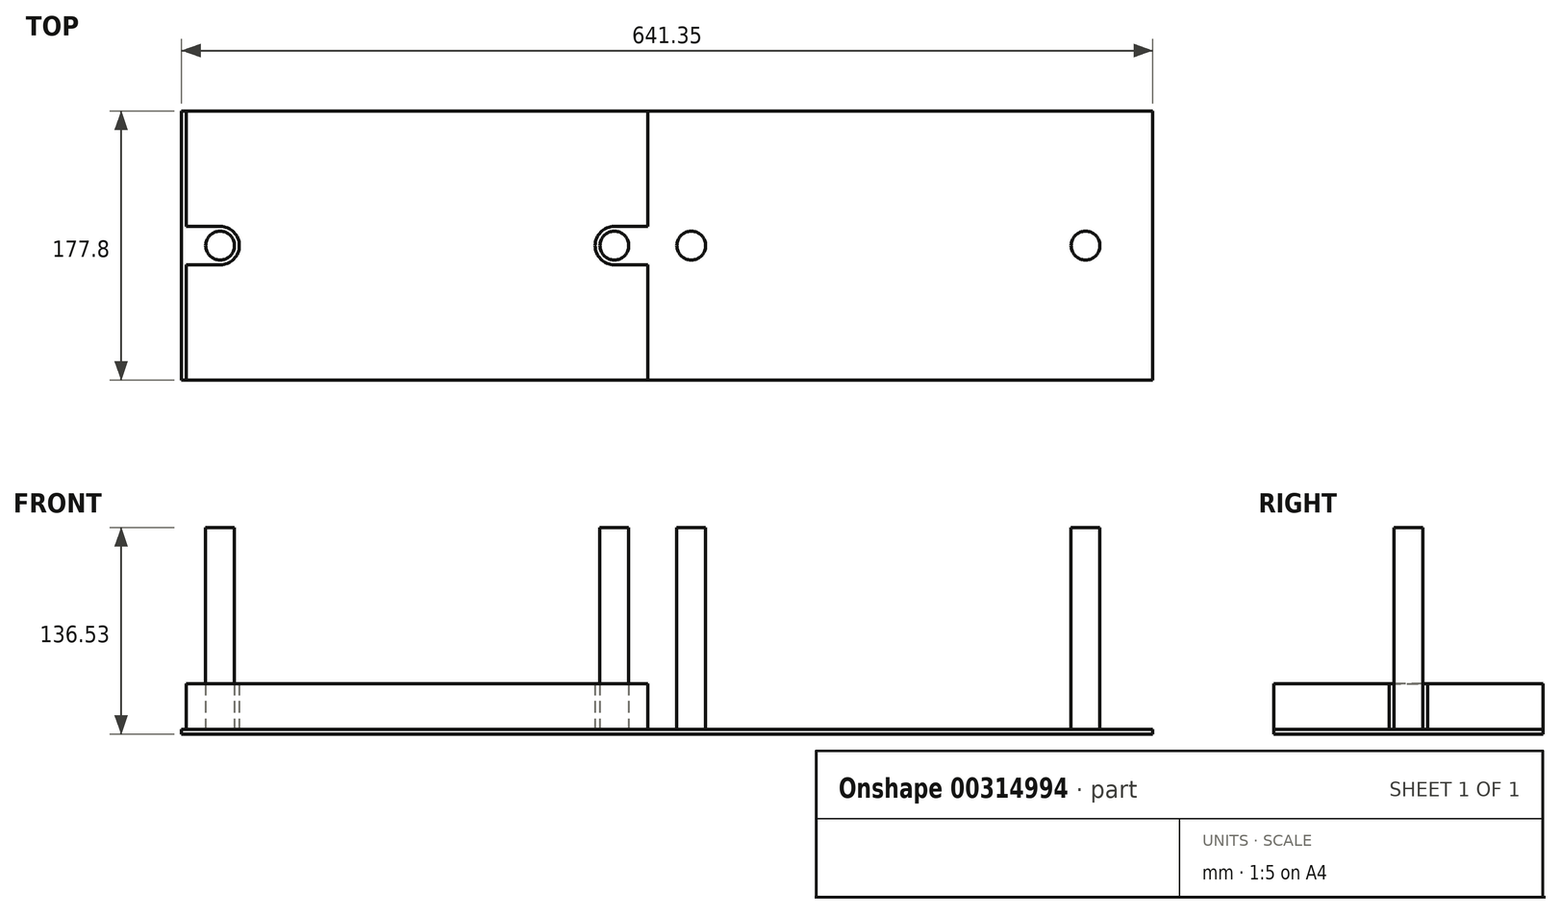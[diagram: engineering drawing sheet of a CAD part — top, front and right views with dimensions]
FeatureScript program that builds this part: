
annotation { "Feature Type Name" : "Feature", "Feature Type Description" : "" }
export const myFeature = defineFeature(function(context is Context, id is Id, definition is map)
    precondition{}
    {
        {
            var Q0;
            Q0=qCreatedBy(makeId("Top.planeOp"),FACE);
            var sketch = newSketch(context, id + "F0", { "sketchPlane" : qUnion([Q0])});
            skLineSegment(sketch, "E0.bottom", {"start": v(0, 0) * mm, "end": v(971.55, 0) * mm});
            skLineSegment(sketch, "E0.top", {"start": v(0, -177.8) * mm, "end": v(971.55, -177.8) * mm});
            skLineSegment(sketch, "E0.left", {"start": v(0, 0) * mm, "end": v(0, -177.8) * mm});
            skLineSegment(sketch, "E0.right", {"start": v(971.55, 0) * mm, "end": v(971.55, -177.8) * mm});
            skSolve(sketch);
        }
        {
            var Q0;
            Q0=qSketchRegion(id+"F0",true);
            extrude(context, id + "F1", {"entities" : qUnion([Q0]), "depth" : 3.17 * mm});
        }
        {
            var Q0;
            Q0=makeQuery(id+"F1.opExtrude","CAP_FACE",FACE,{"disambiguationData":[OSD([sQuery(id+"F0.wireOp",EDGE,"E0.bottom"),sQuery(id+"F0.wireOp",EDGE,"E0.top"),sQuery(id+"F0.wireOp",EDGE,"E0.left"),sQuery(id+"F0.wireOp",EDGE,"E0.right")])],"isStart":false});
            var sketch = newSketch(context, id + "F2", { "sketchPlane" : qUnion([Q0])});
            skPoint(sketch, "E1.1", {"position": v(0, 0) * mm});
            skLineSegment(sketch, "E1.2.0", {"start": v(0, 0) * mm, "end": v(0, -177.8) * mm});
            skLineSegment(sketch, "E1.2.2", {"start": v(0, -177.8) * mm, "end": v(0, 0) * mm});
            skLineSegment(sketch, "E1.4.0", {"start": v(0, -177.8) * mm, "end": v(971.55, -177.8) * mm});
            skLineSegment(sketch, "E1.4.2", {"start": v(971.55, -177.8) * mm, "end": v(0, -177.8) * mm});
            skPoint(sketch, "E1.5", {"position": v(0, 0) * mm});
            skLineSegment(sketch, "E1.7.0", {"start": v(0, 0) * mm, "end": v(0, -177.8) * mm});
            skLineSegment(sketch, "E1.7.1", {"start": v(0, -177.8) * mm, "end": v(971.55, -177.8) * mm});
            skLineSegment(sketch, "E1.7.2", {"start": v(971.55, -177.8) * mm, "end": v(971.55, 0) * mm});
            skLineSegment(sketch, "E1.7.3", {"start": v(971.55, 0) * mm, "end": v(0, 0) * mm});
            skLineSegment(sketch, "E1.9", {"start": v(971.55, 0) * mm, "end": v(971.55, -177.8) * mm});
            skPoint(sketch, "E1.10", {"position": v(971.55, -177.8) * mm});
            skLineSegment(sketch, "E1.11", {"start": v(971.55, 0) * mm, "end": v(971.55, -177.8) * mm});
            skPoint(sketch, "E1.12", {"position": v(0, 0) * mm});
            skLineSegment(sketch, "E1.13.0", {"start": v(0, -177.8) * mm, "end": v(0, 0) * mm});
            skLineSegment(sketch, "E1.13.1", {"start": v(0, 0) * mm, "end": v(971.55, 0) * mm});
            skLineSegment(sketch, "E1.13.2", {"start": v(971.55, 0) * mm, "end": v(971.55, -177.8) * mm});
            skLineSegment(sketch, "E1.13.3", {"start": v(971.55, -177.8) * mm, "end": v(0, -177.8) * mm});
            skPoint(sketch, "E1.14", {"position": v(0, -177.8) * mm});
            skLineSegment(sketch, "E1.15.0", {"start": v(971.55, 0) * mm, "end": v(0, 0) * mm});
            skLineSegment(sketch, "E1.15.2", {"start": v(0, 0) * mm, "end": v(971.55, 0) * mm});
            skLineSegment(sketch, "E1.16", {"start": v(0, 0) * mm, "end": v(0, -177.8) * mm});
            skLineSegment(sketch, "E1.17", {"start": v(0, -177.8) * mm, "end": v(971.55, -177.8) * mm});
            skPoint(sketch, "E1.18", {"position": v(0, -177.8) * mm});
            skPoint(sketch, "E1.19", {"position": v(971.55, -177.8) * mm});
            skLineSegment(sketch, "E1.20", {"start": v(0, 0) * mm, "end": v(0, -177.8) * mm});
            skLineSegment(sketch, "E1.21", {"start": v(0, 0) * mm, "end": v(971.55, 0) * mm});
            skPoint(sketch, "E1.22", {"position": v(971.55, 0) * mm});
            skLineSegment(sketch, "E1.23", {"start": v(0, -177.8) * mm, "end": v(971.55, -177.8) * mm});
            skLineSegment(sketch, "E1.24", {"start": v(0, 0) * mm, "end": v(971.55, 0) * mm});
            skPoint(sketch, "E1.25", {"position": v(971.55, 0) * mm});
            skLineSegment(sketch, "E1.26.0", {"start": v(971.55, -177.8) * mm, "end": v(971.55, 0) * mm});
            skLineSegment(sketch, "E1.26.2", {"start": v(971.55, 0) * mm, "end": v(971.55, -177.8) * mm});
            skLineSegment(sketch, "E2", {"start": v(0, -88.9) * mm, "end": v(971.55, -88.9) * mm, "construction": true});
            skCircle(sketch, "E3", {"center": v(43.69, -88.9) * mm, "radius": 9.52 * mm});
            skCircle(sketch, "E4", {"center": v(304.04, -88.9) * mm, "radius": 9.52 * mm});
            skCircle(sketch, "E5", {"center": v(355.6, -88.9) * mm, "radius": 9.52 * mm});
            skCircle(sketch, "E6", {"center": v(615.95, -88.9) * mm, "radius": 9.52 * mm});
            skCircle(sketch, "E7", {"center": v(927.1, -88.9) * mm, "radius": 9.52 * mm});
            skCircle(sketch, "E8", {"center": v(666.75, -88.9) * mm, "radius": 9.52 * mm});
            skLineSegment(sketch, "E9", {"start": v(43.69, -88.9) * mm, "end": v(304.04, -88.9) * mm});
            skLineSegment(sketch, "E10", {"start": v(355.6, -88.9) * mm, "end": v(615.95, -88.9) * mm});
            skLineSegment(sketch, "E11", {"start": v(666.75, -88.9) * mm, "end": v(927.1, -88.9) * mm});
            skLineSegment(sketch, "E12", {"start": v(485.78, 0) * mm, "end": v(485.78, -88.9) * mm, "construction": true});
            skLineSegment(sketch, "E13.0", {"start": v(311.15, 0) * mm, "end": v(311.15, -177.8) * mm});
            skSolve(sketch);
        }
        {
            var Q0;
            Q0=makeQuery(id+"F2.imprint","IMPRINT",FACE,{"disambiguationData":[TD([[makeQuery(id+"F2.imprint","IMPRINT",EDGE,{"derivedFrom":sQuery(id+"F2.wireOp",EDGE,"E3")}),1.0]])]});
            var Q1;
            Q1=makeQuery(id+"F2.imprint","IMPRINT",FACE,{"disambiguationData":[TD([[makeQuery(id+"F2.imprint","IMPRINT",EDGE,{"derivedFrom":sQuery(id+"F2.wireOp",EDGE,"E4")}),1.0]])]});
            var Q2;
            Q2=makeQuery(id+"F2.imprint","IMPRINT",FACE,{"disambiguationData":[TD([[makeQuery(id+"F2.imprint","IMPRINT",EDGE,{"derivedFrom":sQuery(id+"F2.wireOp",EDGE,"E5")}),1.0]])]});
            var Q3;
            Q3=makeQuery(id+"F2.imprint","IMPRINT",FACE,{"disambiguationData":[TD([[makeQuery(id+"F2.imprint","IMPRINT",EDGE,{"derivedFrom":sQuery(id+"F2.wireOp",EDGE,"E6")}),1.0]])]});
            var Q4;
            Q4=makeQuery(id+"F2.imprint","IMPRINT",FACE,{"disambiguationData":[TD([[makeQuery(id+"F2.imprint","IMPRINT",EDGE,{"derivedFrom":sQuery(id+"F2.wireOp",EDGE,"E8")}),1.0]])]});
            var Q5;
            Q5=makeQuery(id+"F2.imprint","IMPRINT",FACE,{"disambiguationData":[TD([[makeQuery(id+"F2.imprint","IMPRINT",EDGE,{"derivedFrom":sQuery(id+"F2.wireOp",EDGE,"E7")}),1.0]])]});
            extrude(context, id + "F3", {"entities" : qUnion([Q0, Q1, Q2, Q3, Q4, Q5]), "operationType" : NewBodyOperationType.ADD, "depth" : 133.35 * mm});
        }
        {
            var Q0;
            Q0=makeQuery(id+"F1.opExtrude","CAP_FACE",FACE,{"disambiguationData":[OSD([sQuery(id+"F0.wireOp",EDGE,"E0.bottom"),sQuery(id+"F0.wireOp",EDGE,"E0.top"),sQuery(id+"F0.wireOp",EDGE,"E0.left"),sQuery(id+"F0.wireOp",EDGE,"E0.right")])],"isStart":true});
            var sketch = newSketch(context, id + "F4", { "sketchPlane" : qUnion([Q0])});
            skLineSegment(sketch, "E14.bottom", {"start": v(0, 0) * mm, "end": v(330.2, 0) * mm});
            skLineSegment(sketch, "E14.top", {"start": v(0, 177.8) * mm, "end": v(330.2, 177.8) * mm});
            skLineSegment(sketch, "E14.left", {"start": v(0, 0) * mm, "end": v(0, 177.8) * mm});
            skLineSegment(sketch, "E14.right", {"start": v(330.2, 0) * mm, "end": v(330.2, 177.8) * mm});
            skSolve(sketch);
        }
        {
            var Q0;
            Q0 = qSketchRegion(id + "F4", true);
            extrude(context, id + "F5", {"entities" : qUnion([Q0]), "operationType" : NewBodyOperationType.REMOVE, "endBound" : BoundingType.THROUGH_ALL, "oppositeDirection" : true, "depth" : 25.4 * mm});
        }
        {
            var Q0;
            Q0=makeQuery(id+"F1.opExtrude","CAP_FACE",FACE,{"disambiguationData":[OSD([sQuery(id+"F0.wireOp",EDGE,"E0.bottom"),sQuery(id+"F0.wireOp",EDGE,"E0.top"),sQuery(id+"F0.wireOp",EDGE,"E0.left"),sQuery(id+"F0.wireOp",EDGE,"E0.right")])],"isStart":false});
            var sketch = newSketch(context, id + "F6", { "sketchPlane" : qUnion([Q0])});
            skLineSegment(sketch, "E15.bottom", {"start": v(333.38, 0) * mm, "end": v(638.18, 0) * mm});
            skLineSegment(sketch, "E15.top", {"start": v(333.38, -177.8) * mm, "end": v(638.18, -177.8) * mm});
            skLineSegment(sketch, "E15.left", {"start": v(333.38, 0) * mm, "end": v(333.38, -76.2) * mm});
            skLineSegment(sketch, "E15.right", {"start": v(638.18, 0) * mm, "end": v(638.18, -76.2) * mm});
            skCircle(sketch, "E16.0", {"center": v(355.6, -88.9) * mm, "radius": 9.52 * mm, "construction": true});
            skCircle(sketch, "E17.0", {"center": v(615.95, -88.9) * mm, "radius": 9.52 * mm, "construction": true});
            skLineSegment(sketch, "E18", {"start": v(355.6, -79.38) * mm, "end": v(333.38, -79.38) * mm, "construction": true});
            skLineSegment(sketch, "E19", {"start": v(333.38, -98.43) * mm, "end": v(355.6, -98.43) * mm, "construction": true});
            skLineSegment(sketch, "E20.0", {"start": v(355.6, -76.2) * mm, "end": v(333.38, -76.2) * mm});
            skArc(sketch, "E21.0", {"start": v(355.6, -101.6) * mm, "mid": v(368.3, -88.9) * mm, "end": v(355.6, -76.2) * mm});
            skLineSegment(sketch, "E22.0", {"start": v(333.38, -101.6) * mm, "end": v(355.6, -101.6) * mm});
            skLineSegment(sketch, "E23", {"start": v(485.78, -177.8) * mm, "end": v(485.78, 0) * mm, "construction": true});
            skArc(sketch, "E24.MirrorC", {"start": v(615.95, -101.6) * mm, "mid": v(603.25, -88.9) * mm, "end": v(615.95, -76.2) * mm});
            skLineSegment(sketch, "E25.MirrorCS", {"start": v(615.95, -79.38) * mm, "end": v(638.18, -79.38) * mm, "construction": true});
            skLineSegment(sketch, "E26.MirrorCS", {"start": v(615.95, -76.2) * mm, "end": v(638.18, -76.2) * mm});
            skLineSegment(sketch, "E27.MirrorCS", {"start": v(638.18, -101.6) * mm, "end": v(615.95, -101.6) * mm});
            skLineSegment(sketch, "E28.MirrorCS", {"start": v(638.18, -98.43) * mm, "end": v(615.95, -98.43) * mm, "construction": true});
            skLineSegment(sketch, "E29.trimOffspring", {"start": v(333.38, -101.6) * mm, "end": v(333.38, -177.8) * mm});
            skLineSegment(sketch, "E30.trimOffspring", {"start": v(638.18, -101.6) * mm, "end": v(638.18, -177.8) * mm});
            skSolve(sketch);
        }
        {
            var Q0;
            Q0 = qSketchRegion(id + "F6", true);
            extrude(context, id + "F7", {"entities" : qUnion([Q0]), "depth" : 30.16 * mm});
        }
    });
